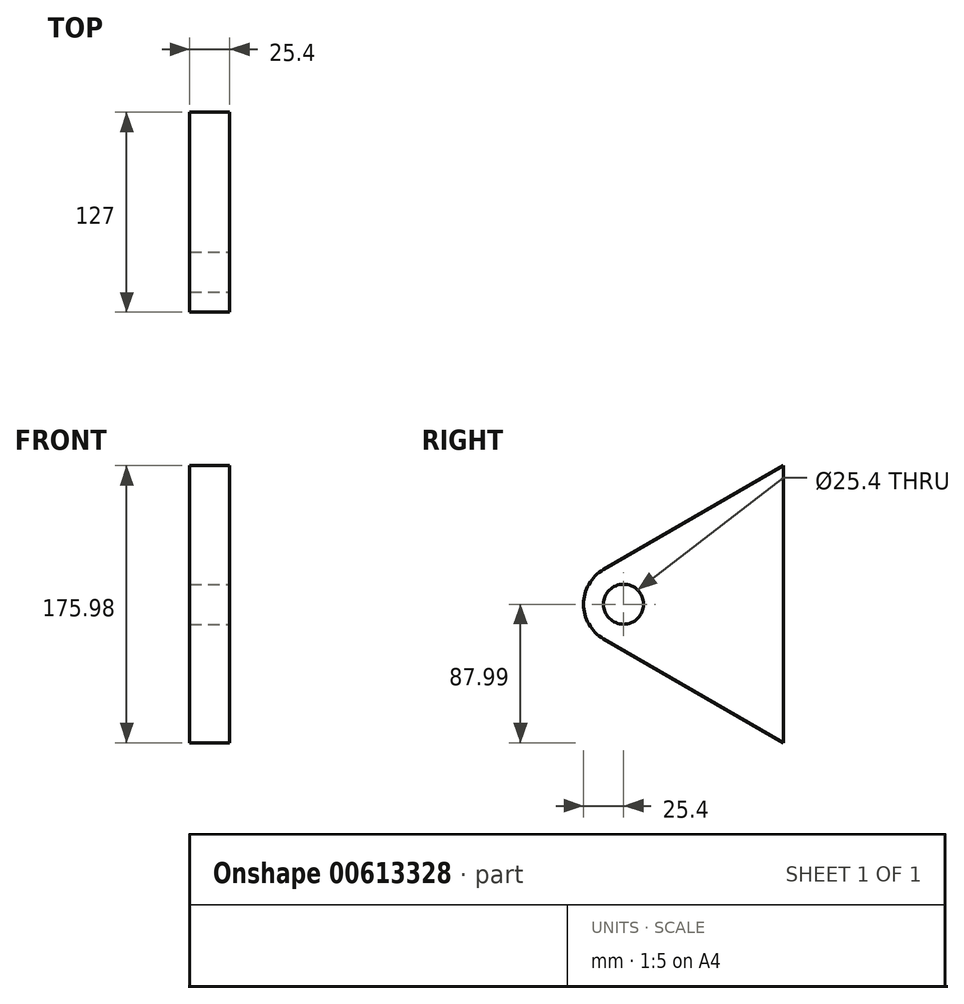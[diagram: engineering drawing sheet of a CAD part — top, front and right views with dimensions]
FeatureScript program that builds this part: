
annotation { "Feature Type Name" : "Feature", "Feature Type Description" : "" }
export const myFeature = defineFeature(function(context is Context, id is Id, definition is map)
    precondition{}
    {
        {
            var Q0;
            Q0=qCreatedBy(makeId("Right.planeOp"),FACE);
            var sketch = newSketch(context, id + "F0", { "sketchPlane" : qUnion([Q0])});
            skLineSegment(sketch, "E0.left", {"start": v(50.8, 76.2) * mm, "end": v(50.8, -76.2) * mm});
            skPoint(sketch, "E0.middle", {"position": v(0, 0) * mm});
            skCircle(sketch, "E1.cCircle", {"center": v(0, 0) * mm, "radius": 50.8 * mm, "construction": true});
            skLineSegment(sketch, "E1.0", {"start": v(50.8, 87.99) * mm, "end": v(50.8, -87.99) * mm});
            skLineSegment(sketch, "E1.1", {"start": v(50.8, -87.99) * mm, "end": v(-101.6, 0) * mm});
            skLineSegment(sketch, "E1.2", {"start": v(-101.6, 0) * mm, "end": v(50.8, 87.99) * mm});
            skPoint(sketch, "E1.0.midPoint", {"position": v(50.8, 0) * mm});
            skPoint(sketch, "E2.orphan", {"position": v(-50.8, -76.2) * mm});
            skPoint(sketch, "E3.orphan", {"position": v(-50.8, 76.2) * mm});
            skSolve(sketch);
        }
        {
            var Q0;
            Q0 = qSketchRegion(id + "F0", true);
            extrude(context, id + "F1", {"entities" : qUnion([Q0]), "depth" : 25.4 * mm, "offsetDistance" : 25.4 * mm});
        }
        {
            var Q0;
            Q0=makeQuery(id+"F1.opExtrude","SWEPT_EDGE",EDGE,{"disambiguationData":[OSD([sQuery(id+"F0.wireOp",EDGE,"E1.1"),sQuery(id+"F0.wireOp",EDGE,"E1.2")])]});
            fillet(context, id + "F2", {"entities" : qUnion([Q0]), "radius" : 25.4 * mm, "tangentPropagation" : true, "allowEdgeOverflow" : false});
        }
        {
            var Q0;
            Q0=makeQuery(id+"F1.opExtrude","CAP_FACE",FACE,{"disambiguationData":[OSD([sQuery(id+"F0.wireOp",EDGE,"E1.0"),sQuery(id+"F0.wireOp",EDGE,"E1.1"),sQuery(id+"F0.wireOp",EDGE,"E1.2")])],"isStart":false});
            var sketch = newSketch(context, id + "F3", { "sketchPlane" : qUnion([Q0])});
            skCircle(sketch, "E4", {"center": v(-50.8, 0) * mm, "radius": 12.7 * mm});
            skSolve(sketch);
        }
        {
            var Q0;
            Q0=makeQuery(id+"F3.imprint","IMPRINT",FACE,{"disambiguationData":[TD([[makeQuery(id+"F3.imprint","IMPRINT",EDGE,{"derivedFrom":sQuery(id+"F3.wireOp",EDGE,"E4")}),1.0]])]});
            extrude(context, id + "F4", {"entities" : qUnion([Q0]), "operationType" : NewBodyOperationType.REMOVE, "oppositeDirection" : true, "depth" : 25.4 * mm, "offsetDistance" : 25.4 * mm});
        }
    });
